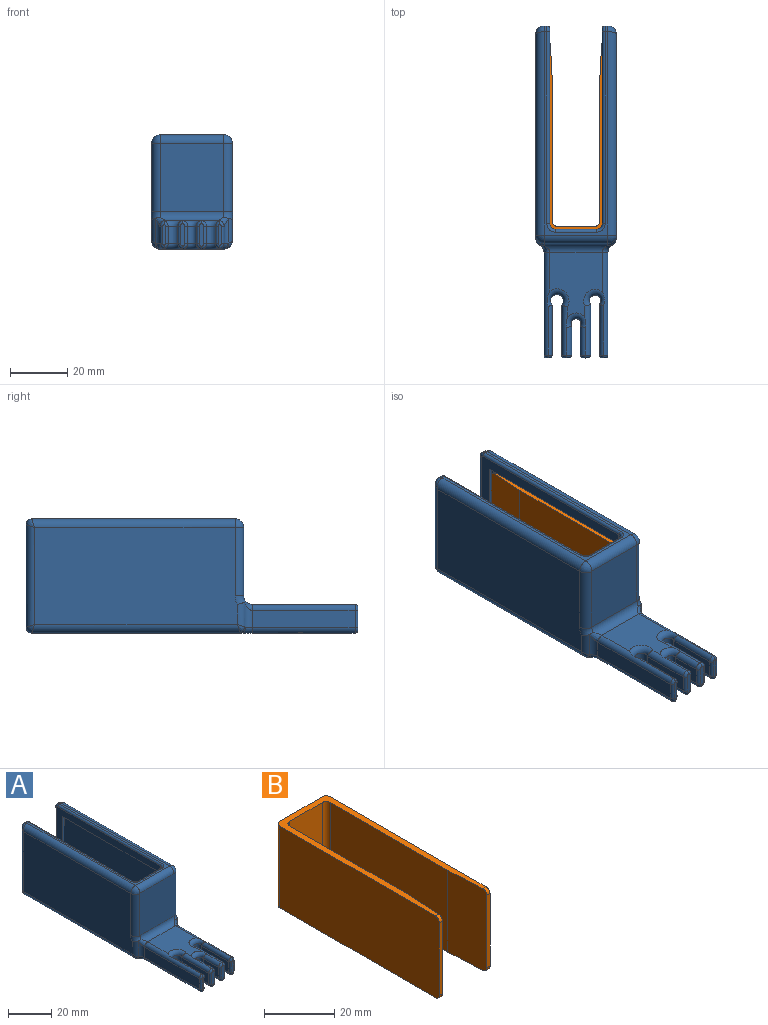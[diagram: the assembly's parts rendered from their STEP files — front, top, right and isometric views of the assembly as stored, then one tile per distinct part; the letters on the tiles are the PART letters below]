
ASSEMBLY  parts=2 mates=1
PART A: 136 faces, bbox 28.4x116.4x40.3 mm
  f0: plane 7.6x0.8mm, normal (0,-1,0), area 5.7mm2, adj f96,f97,f98,f99,f100,f101
  f1: plane 7.93x1.49mm, normal (0,-1,0), area 11mm2, adj f102,f103,f104,f105,f106,f107
  f2: plane 7.97x1.64mm, normal (0,-1,0), area 12.2mm2, adj f114,f115,f116,f117,f118,f119
  f3: plane 100.14x22.37mm, normal (0,0,-1), area 583.5mm2, adj f37,f50,f52,f56,f81,f83,f84,f86
  f4: plane 22.94x18.37mm, normal (0,0,1), area 293.8mm2, adj f35,f68,f69,f71,f74,f75,f77,f78
  f5: plane 24x22.37mm, normal (0,-1,0), area 536.9mm2, adj f35,f42,f44,f47
  f6: plane 14.37x4mm, normal (0,1,0), area 57.5mm2, adj f17,f62,f63,f120
  f7: plane 68.2x38mm, normal (-1,0,0), area 665.2mm2, adj f16,f17,f19,f60,f63,f123,f125,f127
  f8: plane 68.2x38mm, normal (1,0,0), area 665.2mm2, adj f15,f17,f19,f61,f62,f124,f126,f128
  f9: plane 14.37x4mm, normal (0,1,0), area 57.5mm2, adj f19,f60,f61,f135
  f10: plane 71x34mm, normal (1,0,0), area 2393.2mm2, adj f37,f38,f39,f40,f41,f42
  f11: plane 71x34mm, normal (-1,0,0), area 2393.2mm2, adj f46,f47,f48,f49,f50,f51
  f12: plane 71.2x22.37mm, normal (0,0,1), area 166.6mm2, adj f41,f44,f46,f54,f58,f120,f121,f122
  f13: plane 36x1mm, normal (0,1,0), area 36mm2, adj f39,f52,f54,f127
  f14: plane 36x1mm, normal (0,1,0), area 36mm2, adj f48,f56,f58,f128
  f15: plane 30x1mm, normal (0,-1,0), area 30mm2, adj f8,f17,f19,f20
  f16: plane 30x1mm, normal (0,-1,0), area 30mm2, adj f7,f17,f18,f19
  f17: plane 67.2x20.37mm, normal (0,0,-1), area 153.4mm2, adj f6,f7,f8,f15,f16,f18,f20,f21
  f18: plane 65.6x30mm, normal (-1,0,0), area 1968mm2, adj f16,f17,f19,f64
  f19: plane 67.2x20.37mm, normal (0,0,1), area 153.4mm2, adj f7,f8,f9,f15,f16,f18,f20,f21
  f20: plane 65.6x30mm, normal (1,0,0), area 1968mm2, adj f15,f17,f19,f65
  f21: plane 30x17.17mm, normal (0,1,0), area 515.1mm2, adj f17,f19,f64,f65
  f22: plane 36x6mm, normal (-1,0,0), area 216mm2, adj f34,f68,f92,f97
  f23: plane 36x6mm, normal (1,0,0), area 216mm2, adj f36,f75,f83,f110
  f24: plane 7.7x0.95mm, normal (0,-1,0), area 6.8mm2, adj f108,f109,f110,f111,f112,f113
  f25: plane 17.74x6mm, normal (-1,0,0), area 106.4mm2, adj f26,f76,f82,f111
  f26: cylinder r=2mm len=6mm, axis (0,0,1), area 54.1mm2, adj f25,f27,f78,f84
  f27: plane 17.74x6mm, normal (1,0,0), area 106.4mm2, adj f26,f77,f86,f118
  f28: plane 10.1x6mm, normal (-1,0,0), area 60.6mm2, adj f29,f73,f85,f115
  f29: cylinder r=1.75mm len=6mm, axis (0,0,1), area 44.3mm2, adj f28,f30,f74,f88
  f30: plane 10.1x6mm, normal (1,0,0), area 60.6mm2, adj f29,f70,f87,f106
  f31: plane 17.53x6mm, normal (-1,0,0), area 105.2mm2, adj f32,f71,f89,f103
  f32: cylinder r=2.25mm len=6mm, axis (0,0,1), area 61.7mm2, adj f31,f33,f69,f91
  f33: plane 17.53x6mm, normal (1,0,0), area 105.2mm2, adj f32,f67,f90,f100
  f34: cylinder r=3mm len=8.5mm, axis (0,0,-1), area 21.5mm2, adj f22,f51,f66,f93,f94
  f35: cylinder r=3mm len=22.37mm, axis (-1,0,0), area 99.9mm2, adj f4,f5,f40,f49,f66,f72
  f36: cylinder r=3mm len=8.5mm, axis (0,0,1), area 21.5mm2, adj f23,f38,f72,f80,f81
  f37: cylinder r=3mm len=73.2mm, axis (0,1,0), area 339.9mm2, adj f3,f10,f53,f79,f80
  f38: cylinder r=3mm len=8.65mm, axis (0,0,1), area 24.6mm2, adj f10,f36,f40,f72,f79
  f39: cylinder r=3mm len=36mm, axis (0,0,1), area 164.9mm2, adj f10,f13,f53,f55
  f40: torus R=6mm, axis (-1,0,0), area 12mm2, adj f10,f35,f38,f42,f72
  f41: cylinder r=3mm len=71.2mm, axis (0,-1,0), area 333.2mm2, adj f10,f12,f43,f55
  f42: cylinder r=3mm len=24mm, axis (0,0,1), area 113.1mm2, adj f5,f10,f40,f43
  f43: sphere r=3mm, area 14.1mm2, adj f41,f42,f44
  f44: cylinder r=3mm len=22.37mm, axis (-1,0,0), area 105.4mm2, adj f5,f12,f43,f45
  f45: sphere r=3mm, area 14.1mm2, adj f44,f46,f47
  f46: cylinder r=3mm len=71.2mm, axis (0,1,0), area 333.2mm2, adj f11,f12,f45,f59
  f47: cylinder r=3mm len=24mm, axis (0,0,-1), area 113.1mm2, adj f5,f11,f45,f49
  f48: cylinder r=3mm len=36mm, axis (0,0,-1), area 164.9mm2, adj f11,f14,f57,f59
  f49: torus R=6mm, axis (-1,0,0), area 12mm2, adj f11,f35,f47,f51,f66
  f50: cylinder r=3mm len=73.2mm, axis (0,-1,0), area 339.9mm2, adj f3,f11,f57,f94,f95
  f51: cylinder r=3mm len=8.65mm, axis (0,0,-1), area 24.6mm2, adj f11,f34,f49,f66,f95
  f52: cylinder r=2mm len=2mm, axis (1,0,0), area 3.1mm2, adj f3,f13,f53,f129
  f53: bspline ~3.16x3mm, area 6.5mm2, adj f37,f39,f52
  f54: cylinder r=2mm len=2mm, axis (-1,0,0), area 3.1mm2, adj f12,f13,f55,f125
  f55: bspline ~3.16x3mm, area 6.5mm2, adj f39,f41,f54
  f56: cylinder r=2mm len=2mm, axis (1,0,0), area 3.1mm2, adj f3,f14,f57,f130
  f57: bspline ~3.16x3mm, area 6.5mm2, adj f48,f50,f56
  f58: cylinder r=2mm len=2mm, axis (-1,0,0), area 3.1mm2, adj f12,f14,f59,f126
  f59: bspline ~3.16x3mm, area 6.5mm2, adj f46,f48,f58
  f60: cylinder r=2mm len=4mm, axis (0,0,-1), area 12.6mm2, adj f7,f9,f19,f133
  f61: cylinder r=2mm len=4mm, axis (0,0,1), area 12.6mm2, adj f8,f9,f19,f134
  f62: cylinder r=2mm len=4mm, axis (0,0,1), area 12.6mm2, adj f6,f8,f17,f122
  f63: cylinder r=2mm len=4mm, axis (0,0,-1), area 12.6mm2, adj f6,f7,f17,f121
  f64: cylinder r=1.6mm len=30mm, axis (0,0,-1), area 75.4mm2, adj f17,f18,f19,f21
  f65: cylinder r=1.6mm len=30mm, axis (0,0,1), area 75.4mm2, adj f17,f19,f20,f21
  f66: bspline ~3.94x3.94mm, area 8.7mm2, adj f34,f35,f49,f51,f68
  f67: cylinder r=2mm len=17.53mm, axis (0,1,0), area 43.8mm2, adj f33,f68,f69,f98
  f68: cylinder r=2mm len=36mm, axis (0,1,0), area 99.1mm2, adj f4,f22,f66,f67,f69,f96
  f69: torus R=4.25mm, axis (0,0,1), area 36.7mm2, adj f4,f32,f67,f68,f71
  f70: cylinder r=2mm len=10.1mm, axis (0,1,0), area 28.5mm2, adj f30,f71,f74,f104
  f71: cylinder r=2mm len=17.53mm, axis (0,-1,0), area 50.6mm2, adj f4,f31,f69,f70,f74,f102
  f72: bspline ~3.94x3.94mm, area 8.7mm2, adj f35,f36,f38,f40,f75
  f73: cylinder r=2mm len=10.1mm, axis (0,-1,0), area 29.3mm2, adj f28,f74,f77,f114
  f74: torus R=3.75mm, axis (0,0,1), area 29.4mm2, adj f4,f29,f70,f71,f73,f77
  f75: cylinder r=2mm len=36mm, axis (0,-1,0), area 101.1mm2, adj f4,f23,f72,f76,f78,f108
  f76: cylinder r=2mm len=17.74mm, axis (0,-1,0), area 45.7mm2, adj f25,f75,f78,f109
  f77: cylinder r=2mm len=17.74mm, axis (0,1,0), area 52.3mm2, adj f4,f27,f73,f74,f78,f116
  f78: torus R=4mm, axis (0,0,1), area 33.7mm2, adj f4,f26,f75,f76,f77
  f79: bspline ~2.69x2.69mm, area 3mm2, adj f37,f38,f80
  f80: bspline ~2.37x2.23mm, area 2.9mm2, adj f36,f37,f79,f81
  f81: torus R=5mm, axis (0,0,1), area 10.9mm2, adj f3,f36,f80,f83
  f82: cylinder r=2mm len=17.74mm, axis (0,-1,0), area 45.7mm2, adj f25,f83,f84,f113
  f83: cylinder r=2mm len=36mm, axis (0,1,0), area 101.1mm2, adj f3,f23,f81,f82,f84,f112
  f84: torus R=4mm, axis (0,0,1), area 33.7mm2, adj f3,f26,f82,f83,f86
  f85: cylinder r=2mm len=10.1mm, axis (0,-1,0), area 29.3mm2, adj f28,f86,f88,f117
  f86: cylinder r=2mm len=17.74mm, axis (0,1,0), area 52.3mm2, adj f3,f27,f84,f85,f88,f119
  f87: cylinder r=2mm len=10.1mm, axis (0,1,0), area 28.5mm2, adj f30,f88,f89,f107
  f88: torus R=3.75mm, axis (0,0,1), area 29.4mm2, adj f3,f29,f85,f86,f87,f89
  f89: cylinder r=2mm len=17.53mm, axis (0,-1,0), area 50.6mm2, adj f3,f31,f87,f88,f91,f105
  f90: cylinder r=2mm len=17.53mm, axis (0,1,0), area 43.8mm2, adj f33,f91,f92,f101
  f91: torus R=4.25mm, axis (0,0,1), area 36.7mm2, adj f3,f32,f89,f90,f92
  f92: cylinder r=2mm len=36mm, axis (0,-1,0), area 99.1mm2, adj f3,f22,f90,f91,f93,f99
  f93: torus R=5mm, axis (0,0,1), area 10.9mm2, adj f3,f34,f92,f94
  f94: bspline ~2.37x2.23mm, area 2.9mm2, adj f34,f50,f93,f95
  f95: bspline ~2.69x2.69mm, area 3mm2, adj f50,f51,f94
  f96: torus R=1mm, axis (0,-1,0), area 2.9mm2, adj f0,f68,f97,f98
  f97: cylinder r=1mm len=6mm, axis (0,0,1), area 9.4mm2, adj f0,f22,f96,f99
  f98: torus R=1mm, axis (0,-1,0), area 2.9mm2, adj f0,f67,f96,f100
  f99: torus R=1mm, axis (0,-1,0), area 2.9mm2, adj f0,f92,f97,f101
  f100: cylinder r=1mm len=6mm, axis (0,0,-1), area 9.4mm2, adj f0,f33,f98,f101
  f101: torus R=1mm, axis (0,-1,0), area 2.9mm2, adj f0,f90,f99,f100
  f102: torus R=1mm, axis (0,-1,0), area 3.6mm2, adj f1,f71,f103,f104
  f103: cylinder r=1mm len=6mm, axis (0,0,1), area 9.4mm2, adj f1,f31,f102,f105
  f104: torus R=1mm, axis (0,-1,0), area 3.6mm2, adj f1,f70,f102,f106
  f105: torus R=1mm, axis (0,-1,0), area 3.6mm2, adj f1,f89,f103,f107
  f106: cylinder r=1mm len=6mm, axis (0,0,-1), area 9.4mm2, adj f1,f30,f104,f107
  f107: torus R=1mm, axis (0,-1,0), area 3.6mm2, adj f1,f87,f105,f106
  f108: torus R=1mm, axis (0,-1,0), area 3mm2, adj f24,f75,f109,f110
  f109: torus R=1mm, axis (0,-1,0), area 3mm2, adj f24,f76,f108,f111
  f110: cylinder r=1mm len=6mm, axis (0,0,-1), area 9.4mm2, adj f23,f24,f108,f112
  f111: cylinder r=1mm len=6mm, axis (0,0,1), area 9.4mm2, adj f24,f25,f109,f113
  f112: torus R=1mm, axis (0,-1,0), area 3mm2, adj f24,f83,f110,f113
  f113: torus R=1mm, axis (0,-1,0), area 3mm2, adj f24,f82,f111,f112
  f114: torus R=1mm, axis (0,-1,0), area 3.7mm2, adj f2,f73,f115,f116
  f115: cylinder r=1mm len=6mm, axis (0,0,1), area 9.4mm2, adj f2,f28,f114,f117
  f116: torus R=1mm, axis (0,-1,0), area 3.7mm2, adj f2,f77,f114,f118
  f117: torus R=1mm, axis (0,-1,0), area 3.7mm2, adj f2,f85,f115,f119
  f118: cylinder r=1mm len=6mm, axis (0,0,-1), area 9.4mm2, adj f2,f27,f116,f119
  f119: torus R=1mm, axis (0,-1,0), area 3.7mm2, adj f2,f86,f117,f118
  f120: cylinder r=1mm len=14.37mm, axis (1,0,0), area 22.6mm2, adj f6,f12,f121,f122
  f121: torus R=3mm, axis (0,0,1), area 5.8mm2, adj f12,f63,f120,f123
  f122: torus R=3mm, axis (0,0,1), area 5.8mm2, adj f12,f62,f120,f124
  f123: cylinder r=1mm len=67.2mm, axis (0,-1,0), area 105.6mm2, adj f7,f12,f121,f125
  f124: cylinder r=1mm len=67.2mm, axis (0,1,0), area 105.6mm2, adj f8,f12,f122,f126
  f125: torus R=1mm, axis (-1,0,0), area 4mm2, adj f7,f54,f123,f127
  f126: torus R=1mm, axis (-1,0,0), area 4mm2, adj f8,f58,f124,f128
  f127: cylinder r=1mm len=36mm, axis (0,0,-1), area 56.5mm2, adj f7,f13,f125,f129
  f128: cylinder r=1mm len=36mm, axis (0,0,1), area 56.5mm2, adj f8,f14,f126,f130
  f129: torus R=1mm, axis (-1,0,0), area 4mm2, adj f7,f52,f127,f131
  f130: torus R=1mm, axis (-1,0,0), area 4mm2, adj f8,f56,f128,f132
  f131: cylinder r=1mm len=67.2mm, axis (0,1,0), area 105.6mm2, adj f3,f7,f129,f133
  f132: cylinder r=1mm len=67.2mm, axis (0,-1,0), area 105.6mm2, adj f3,f8,f130,f134
  f133: torus R=3mm, axis (0,0,1), area 5.8mm2, adj f3,f60,f131,f135
  f134: torus R=3mm, axis (0,0,1), area 5.8mm2, adj f3,f61,f132,f135
  f135: cylinder r=1mm len=14.37mm, axis (-1,0,0), area 22.6mm2, adj f3,f9,f133,f134
PART B: 20 faces, bbox 20.4x66x28.5 mm
  f0: plane 25.3x1.21mm, normal (0,-1,0), area 30.7mm2, adj f4,f11,f12,f13
  f1: plane 64.4x20.37mm, normal (0,0,1), area 280.9mm2, adj f3,f4,f6,f7,f8,f9,f10,f11
  f2: plane 64.4x20.37mm, normal (0,0,-1), area 280.9mm2, adj f3,f4,f6,f7,f8,f9,f10,f11
  f3: plane 64.4x28.5mm, normal (-1,0,0), area 1834.3mm2, adj f1,f2,f5,f16,f18,f19
  f4: plane 64.4x28.5mm, normal (1,0,0), area 1834.3mm2, adj f0,f1,f2,f12,f13,f17
  f5: plane 25.3x1.21mm, normal (0,-1,0), area 30.7mm2, adj f3,f10,f18,f19
  f6: plane 28.5x17.17mm, normal (0,1,0), area 489.3mm2, adj f1,f2,f16,f17
  f7: plane 28.5x13.17mm, normal (0,-1,0), area 375.3mm2, adj f1,f2,f14,f15
  f8: plane 47.4x28.5mm, normal (1,0,0), area 1350.9mm2, adj f1,f2,f10,f14
  f9: plane 47.4x28.5mm, normal (-1,0,0), area 1350.9mm2, adj f1,f2,f11,f15
  f10: plane 28.5x15mm, normal (1,-0.05,0), area 427mm2, adj f1,f2,f5,f8,f18,f19
  f11: plane 28.5x15mm, normal (-1,-0.05,0), area 427mm2, adj f0,f1,f2,f9,f12,f13
  f12: cylinder r=1.6mm len=1.6mm, axis (-1,0,0), area 3.1mm2, adj f0,f2,f4,f11
  f13: cylinder r=1.6mm len=1.6mm, axis (1,0,0), area 3.1mm2, adj f0,f1,f4,f11
  f14: cylinder r=1.6mm len=28.5mm, axis (0,0,1), area 71.6mm2, adj f1,f2,f7,f8
  f15: cylinder r=1.6mm len=28.5mm, axis (0,0,-1), area 71.6mm2, adj f1,f2,f7,f9
  f16: cylinder r=1.6mm len=28.5mm, axis (0,0,-1), area 71.6mm2, adj f1,f2,f3,f6
  f17: cylinder r=1.6mm len=28.5mm, axis (0,0,1), area 71.6mm2, adj f1,f2,f4,f6
  f18: cylinder r=1.6mm len=1.6mm, axis (-1,0,0), area 3.1mm2, adj f2,f3,f5,f10
  f19: cylinder r=1.6mm len=1.6mm, axis (1,0,0), area 3.1mm2, adj f1,f3,f5,f10
PLACE A t=(4.55,-20.31,-8.76)mm
PLACE B rot(axis=(1,0,0),180deg) t=(4.55,-18.81,30.74)mm
MATE cylindrical B.f16 <-> A.f65  axis (0,0,1) through (-4.03,-17.21,11.49)mm
